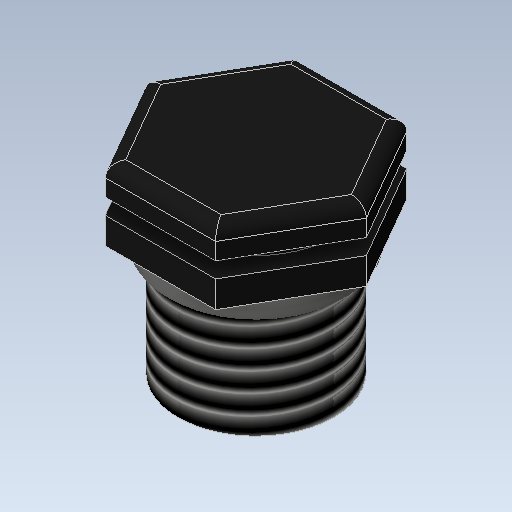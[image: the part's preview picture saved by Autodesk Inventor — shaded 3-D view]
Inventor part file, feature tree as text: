
AUTODESK INVENTOR PART (.ipt)
format: ipt  version: 2021 (Build 250183000, 183)  size: 245,760 bytes
history: native  units: mm
features: sketch x4, revolve x2, extrude x2, thread x1, plane x1, fillet x1, projected_geometry x1
ambient origin geometry x8: Origin, YZ Plane, XZ Plane, XY Plane, X Axis, Y Axis, Z Axis, Center Point
bodies: Solid1 (feature_tree), Solid2 (feature_tree)
feature tree (12):
  revolve  "Revolution1"  [1 undecoded]
  thread  "Thread1"  [1 undecoded]
  revolve  "Revolution2"  Angle=90.0deg
  extrude  "Extrusion1"  Depth=10.0mm
  plane  "Work Plane1"
  extrude  "Extrusion2"  Depth=10.0mm TaperAngle=0.0deg
  fillet  "Fillet2"  [1 undecoded]
  sketch  "Sketch1"  dims[d0=10.0mm d1=5.55mm d2=8.5mm]
  sketch  "Sketch2"  dims[d3=6.0mm d4=90.0deg]
  sketch  "Sketch3"  dims[d6=10.0mm d7=0.0mm d8=2.0mm]
  sketch  "Sketch4"  dims[d9=90.0deg d10=10.0mm d11=0.0mm d12=-3.5mm d13=1.2mm d14=0.0mm d15=1.0mm]
  projected_geometry  "Projected Loop1"
note: 3 required parameter values undecoded (feature->parameter linkage not recoverable at this tier; creation-order binding heuristic only, values carry confidence <= 0.55)